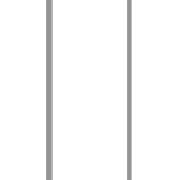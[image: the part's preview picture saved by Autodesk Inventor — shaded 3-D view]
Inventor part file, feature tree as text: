
AUTODESK INVENTOR PART (.ipt)
format: ipt  version: 2021 (Build 250183000, 183)  size: 142,336 bytes
history: native  units: in
note: dims shown in document units (in); Inventor stores cm internally (conversion verified against a paired STEP export)
features: other x4, sketch x4, plane x2, hole x1
ambient origin geometry x8: Origin, YZ Plane, XZ Plane, XY Plane, X Axis, Y Axis, Z Axis, Center Point
bodies: Solid1 (feature_tree), Body (feature_tree)
feature tree (11):
  other  "Driven Length"
  other  "Frame Generator"
  plane  "Work Plane3"
  other  "Start Plane"
  other  "End Plane"
  hole  "Hole2"  [1 undecoded]
  sketch  "Sketch"  dims[d4=2.0in d16=-0.0in d17=2.0in d18=0.12in d19=0.0in d22=1.5in d23=0.4375in d24=0.75in d25=0.635in d26=0.25in d27=0.5635in d28=1.0in d29=0.8108in d32=90.0deg d21=2.0in d8=0.5in d9=0.0344in d10=0.5in d11=0.0344in]
  sketch  "Sketch5"  dims[d0=1.5in d1=1.0in]
  sketch  "Sketch8"  dims[d2=0.0625in]
  plane  "Work Plane6"
  sketch  "Sketch9"  dims[d3=0.0625in]
note: 1 required parameter value undecoded (feature->parameter linkage not recoverable at this tier; creation-order binding heuristic only, values carry confidence <= 0.55)
